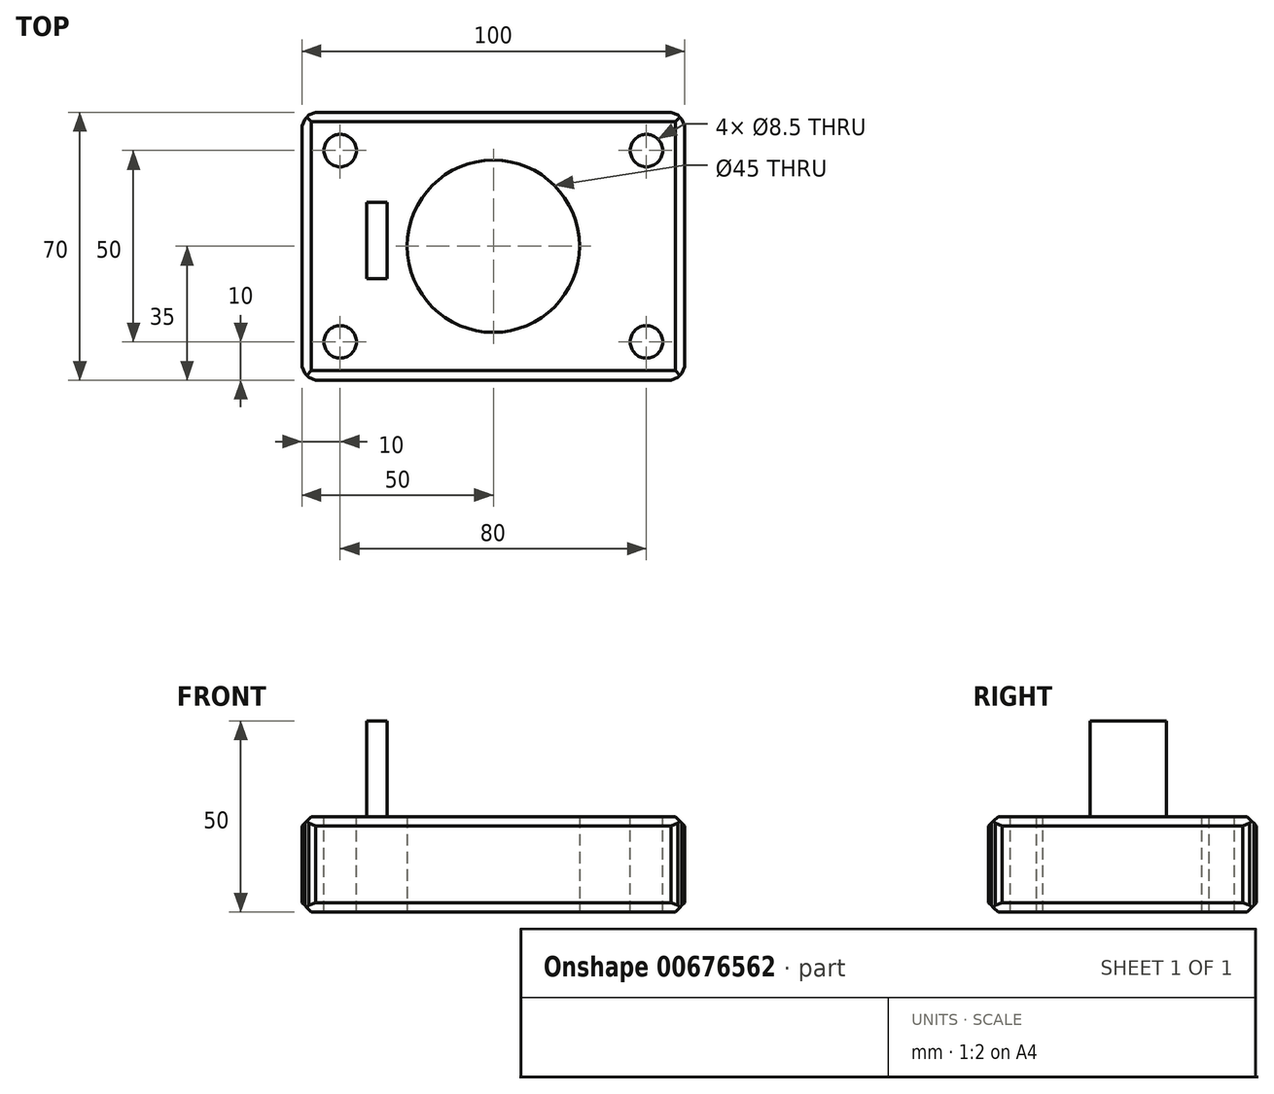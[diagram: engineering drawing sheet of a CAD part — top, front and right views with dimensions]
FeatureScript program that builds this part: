
annotation { "Feature Type Name" : "Feature", "Feature Type Description" : "" }
export const myFeature = defineFeature(function(context is Context, id is Id, definition is map)
    precondition{}
    {
        {
            var Q0;
            Q0=qCreatedBy(makeId("Top.planeOp"),FACE);
            var sketch = newSketch(context, id + "F0", { "sketchPlane" : qUnion([Q0])});
            skLineSegment(sketch, "E0.bottom", {"start": v(50, -35) * mm, "end": v(-50, -35) * mm});
            skLineSegment(sketch, "E0.top", {"start": v(50, 35) * mm, "end": v(-50, 35) * mm});
            skLineSegment(sketch, "E0.left", {"start": v(50, -35) * mm, "end": v(50, 35) * mm});
            skLineSegment(sketch, "E0.right", {"start": v(-50, -35) * mm, "end": v(-50, 35) * mm});
            skPoint(sketch, "E0.middle", {"position": v(0, 0) * mm});
            skCircle(sketch, "E1", {"center": v(0, 0) * mm, "radius": 22.5 * mm});
            skSolve(sketch);
        }
        {
            var Q0;
            Q0 = qSketchRegion(id + "F0", true);
            extrude(context, id + "F1", {"entities" : qUnion([Q0]), "depth" : 25 * mm, "offsetDistance" : 25 * mm});
        }
        {
            var Q0;
            Q0=makeQuery(id+"F1.opExtrude","CAP_FACE",FACE,{"disambiguationData":[OSD([sQuery(id+"F0.wireOp",EDGE,"E0.bottom"),sQuery(id+"F0.wireOp",EDGE,"E0.top"),sQuery(id+"F0.wireOp",EDGE,"E0.left"),sQuery(id+"F0.wireOp",EDGE,"E0.right"),sQuery(id+"F0.wireOp",EDGE,"E1")])],"isStart":false});
            var sketch = newSketch(context, id + "F2", { "sketchPlane" : qUnion([Q0])});
            skCircle(sketch, "E2", {"center": v(-40, 25) * mm, "radius": 4.25 * mm});
            skCircle(sketch, "E3.0.1.0", {"center": v(-40, -25) * mm, "radius": 4.25 * mm});
            skCircle(sketch, "E3.1.0.0", {"center": v(40, 25) * mm, "radius": 4.25 * mm});
            skCircle(sketch, "E3.1.1.0", {"center": v(40, -25) * mm, "radius": 4.25 * mm});
            skLineSegment(sketch, "E3.direction1", {"start": v(-40, 25) * mm, "end": v(40, 25) * mm, "construction": true});
            skLineSegment(sketch, "E3.direction2", {"start": v(-40, 25) * mm, "end": v(-40, -25) * mm, "construction": true});
            skSolve(sketch);
        }
        {
            var Q0;
            Q0=makeQuery(id+"F2.imprint","IMPRINT",FACE,{"disambiguationData":[TD([[makeQuery(id+"F2.imprint","IMPRINT",EDGE,{"derivedFrom":sQuery(id+"F2.wireOp",EDGE,"E2")}),1.0]])]});
            var Q1;
            Q1=makeQuery(id+"F2.imprint","IMPRINT",FACE,{"disambiguationData":[TD([[makeQuery(id+"F2.imprint","IMPRINT",EDGE,{"derivedFrom":sQuery(id+"F2.wireOp",EDGE,"E3.0.1.0")}),1.0]])]});
            var Q2;
            Q2=makeQuery(id+"F2.imprint","IMPRINT",FACE,{"disambiguationData":[TD([[makeQuery(id+"F2.imprint","IMPRINT",EDGE,{"derivedFrom":sQuery(id+"F2.wireOp",EDGE,"E3.1.1.0")}),1.0]])]});
            var Q3;
            Q3=makeQuery(id+"F2.imprint","IMPRINT",FACE,{"disambiguationData":[TD([[makeQuery(id+"F2.imprint","IMPRINT",EDGE,{"derivedFrom":sQuery(id+"F2.wireOp",EDGE,"E3.1.0.0")}),1.0]])]});
            extrude(context, id + "F3", {"entities" : qUnion([Q0, Q1, Q2, Q3]), "operationType" : NewBodyOperationType.REMOVE, "endBound" : BoundingType.THROUGH_ALL, "oppositeDirection" : true, "depth" : 25 * mm, "offsetDistance" : 25 * mm});
        }
        {
            var Q0;
            Q0=makeQuery(id+"F1.opExtrude","SWEPT_EDGE",EDGE,{"disambiguationData":[OSD([sQuery(id+"F0.wireOp",EDGE,"E0.top"),sQuery(id+"F0.wireOp",EDGE,"E0.left")])]});
            var Q1;
            Q1=makeQuery(id+"F1.opExtrude","SWEPT_EDGE",EDGE,{"disambiguationData":[OSD([sQuery(id+"F0.wireOp",EDGE,"E0.bottom"),sQuery(id+"F0.wireOp",EDGE,"E0.left")])]});
            var Q2;
            Q2=makeQuery(id+"F1.opExtrude","SWEPT_EDGE",EDGE,{"disambiguationData":[OSD([sQuery(id+"F0.wireOp",EDGE,"E0.bottom"),sQuery(id+"F0.wireOp",EDGE,"E0.right")])]});
            var Q3;
            Q3=makeQuery(id+"F1.opExtrude","SWEPT_EDGE",EDGE,{"disambiguationData":[OSD([sQuery(id+"F0.wireOp",EDGE,"E0.top"),sQuery(id+"F0.wireOp",EDGE,"E0.right")])]});
            chamfer(context, id + "F4", {"entities" : qUnion([Q0, Q1, Q2, Q3]), "width" : 2.5 * mm});
        }
        {
            var Q0;
            Q0=makeQuery(id+"F1.opExtrude","CAP_EDGE",EDGE,{"disambiguationData":[OSD([sQuery(id+"F0.wireOp",EDGE,"E0.left")])],"isStart":false});
            var Q1;
            Q1=makeQuery(id+"F1.opExtrude","SWEPT_FACE",FACE,{"disambiguationData":[OSD([sQuery(id+"F0.wireOp",EDGE,"E0.left")])]});
            var Q2;
            Q2=makeQuery(id+"F1.opExtrude","SWEPT_FACE",FACE,{"disambiguationData":[OSD([sQuery(id+"F0.wireOp",EDGE,"E0.bottom")])]});
            var Q3;
            Q3=makeQuery(id+"F1.opExtrude","SWEPT_FACE",FACE,{"disambiguationData":[OSD([sQuery(id+"F0.wireOp",EDGE,"E0.right")])]});
            var Q4;
            Q4=makeQuery(id+"F1.opExtrude","SWEPT_FACE",FACE,{"disambiguationData":[OSD([sQuery(id+"F0.wireOp",EDGE,"E0.top")])]});
            chamfer(context, id + "F5", {"entities" : qUnion([Q0, Q1, Q2, Q3, Q4]), "width" : 2.5 * mm, "tangentPropagation" : true});
        }
        {
            var Q0;
            Q0=makeQuery(id+"F2.imprint","IMPRINT",FACE,{"disambiguationData":[TD([[makeQuery(id+"F2.imprint","IMPRINT",EDGE,{"derivedFrom":sQuery(id+"F2.wireOp",EDGE,"E2")}),-1.0]])]});
            var sketch = newSketch(context, id + "F6", { "sketchPlane" : qUnion([Q0])});
            skLineSegment(sketch, "E4.bottom", {"start": v(-33.1, -8.51) * mm, "end": v(-27.79, -8.51) * mm});
            skLineSegment(sketch, "E4.top", {"start": v(-33.1, 11.47) * mm, "end": v(-27.79, 11.47) * mm});
            skLineSegment(sketch, "E4.left", {"start": v(-33.1, -8.51) * mm, "end": v(-33.1, 11.47) * mm});
            skLineSegment(sketch, "E4.right", {"start": v(-27.79, -8.51) * mm, "end": v(-27.79, 11.47) * mm});
            skLineSegment(sketch, "E5.bottom", {"start": v(-32.64, 3.38) * mm, "end": v(-33.1, 3.38) * mm});
            skLineSegment(sketch, "E5.top", {"start": v(-32.64, 1.48) * mm, "end": v(-33.1, 1.48) * mm});
            skLineSegment(sketch, "E5.left", {"start": v(-32.64, 3.38) * mm, "end": v(-32.64, 1.48) * mm});
            skLineSegment(sketch, "E5.right", {"start": v(-33.1, 3.38) * mm, "end": v(-33.1, 1.48) * mm});
            skSolve(sketch);
        }
        {
            var Q0;
            Q0 = qSketchRegion(id + "F6", true);
            extrude(context, id + "F7", {"entities" : qUnion([Q0]), "operationType" : NewBodyOperationType.ADD, "depth" : 25 * mm, "offsetDistance" : 25 * mm});
        }
    });
